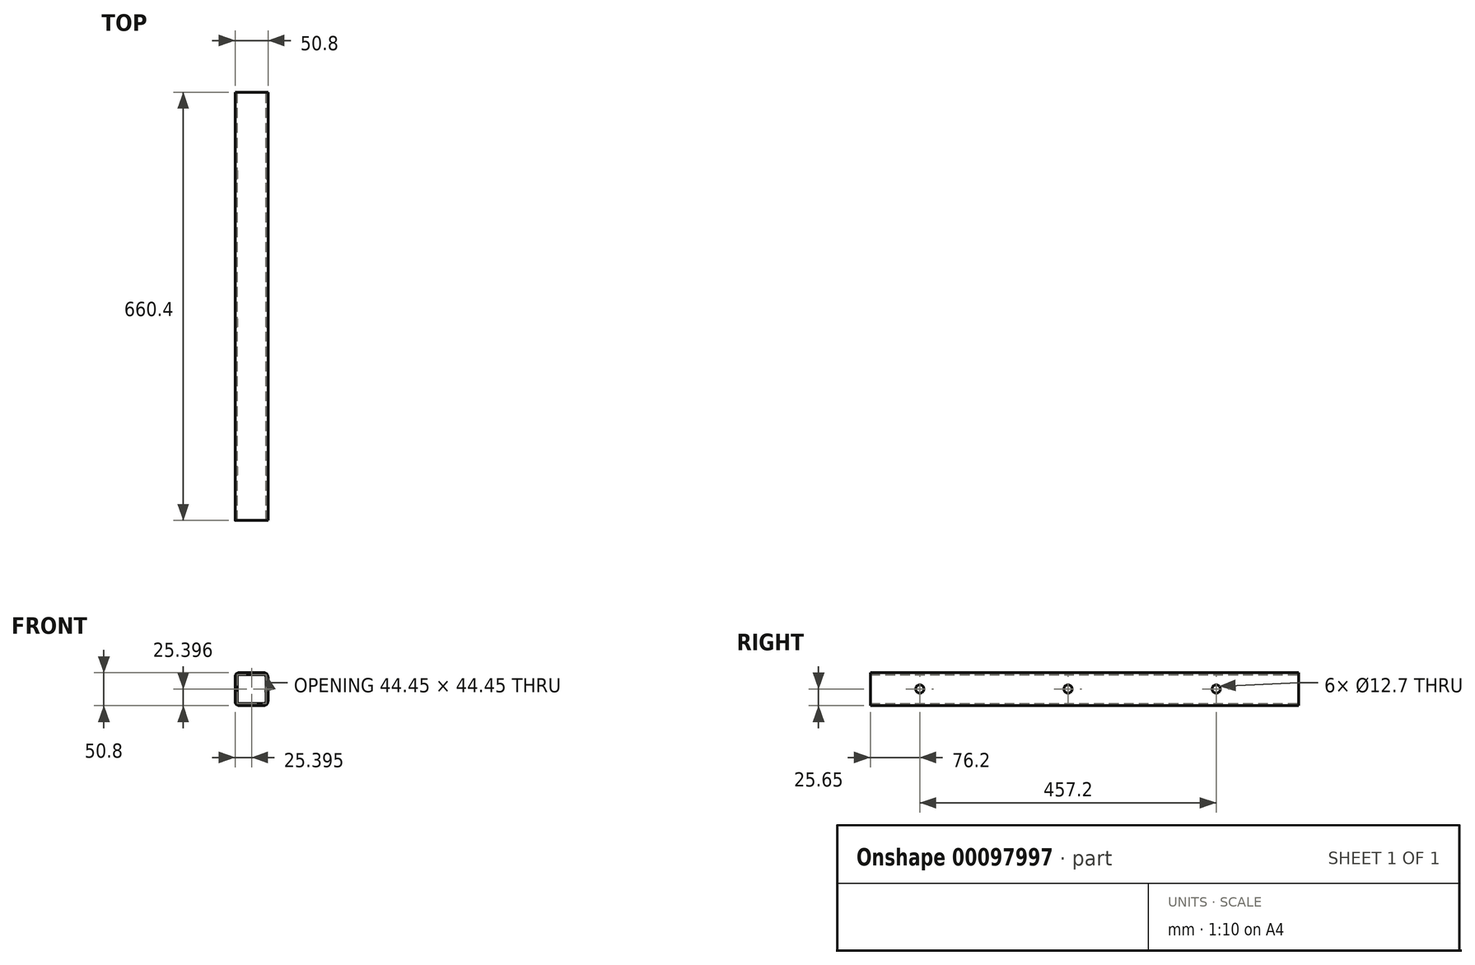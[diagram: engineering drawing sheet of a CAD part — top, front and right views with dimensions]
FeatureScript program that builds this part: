
annotation { "Feature Type Name" : "Feature", "Feature Type Description" : "" }
export const myFeature = defineFeature(function(context is Context, id is Id, definition is map)
    precondition{}
    {
        {
            var Q0;
            Q0=qCreatedBy(makeId("Front.planeOp"),FACE);
            var sketch = newSketch(context, id + "F0", { "sketchPlane" : qUnion([Q0])});
            skLineSegment(sketch, "E0.bottom", {"start": v(18.78, -25.65) * mm, "end": v(-19.32, -25.65) * mm});
            skLineSegment(sketch, "E0.top", {"start": v(18.78, 25.15) * mm, "end": v(-19.32, 25.15) * mm});
            skLineSegment(sketch, "E0.left", {"start": v(25.13, -19.3) * mm, "end": v(25.13, 18.8) * mm});
            skLineSegment(sketch, "E0.right", {"start": v(-25.67, -19.3) * mm, "end": v(-25.67, 18.8) * mm});
            skPoint(sketch, "E0.middle", {"position": v(-0.27, -0.25) * mm});
            skLineSegment(sketch, "E1.bottom", {"start": v(18.78, 21.97) * mm, "end": v(-19.32, 21.97) * mm});
            skLineSegment(sketch, "E1.top", {"start": v(18.78, -22.48) * mm, "end": v(-19.32, -22.48) * mm});
            skLineSegment(sketch, "E1.left", {"start": v(21.95, 18.8) * mm, "end": v(21.95, -19.3) * mm});
            skLineSegment(sketch, "E1.right", {"start": v(-22.5, 18.8) * mm, "end": v(-22.5, -19.3) * mm});
            skPoint(sketch, "E2.visualSharp", {"position": v(-25.67, 25.15) * mm});
            skArc(sketch, "E2.filletArc", {"start": v(-19.32, 25.15) * mm, "mid": v(-23.81, 23.29) * mm, "end": v(-25.67, 18.8) * mm});
            skPoint(sketch, "E3.visualSharp", {"position": v(25.13, 25.15) * mm});
            skArc(sketch, "E3.filletArc", {"start": v(25.13, 18.8) * mm, "mid": v(23.27, 23.29) * mm, "end": v(18.78, 25.15) * mm});
            skPoint(sketch, "E4.visualSharp", {"position": v(25.13, -25.65) * mm});
            skArc(sketch, "E4.filletArc", {"start": v(18.78, -25.65) * mm, "mid": v(23.27, -23.8) * mm, "end": v(25.13, -19.3) * mm});
            skPoint(sketch, "E5.visualSharp", {"position": v(-25.67, -25.65) * mm});
            skArc(sketch, "E5.filletArc", {"start": v(-25.67, -19.3) * mm, "mid": v(-23.81, -23.8) * mm, "end": v(-19.32, -25.65) * mm});
            skPoint(sketch, "E6.visualSharp", {"position": v(21.95, 21.97) * mm});
            skArc(sketch, "E6.filletArc", {"start": v(21.95, 18.8) * mm, "mid": v(21.02, 21.04) * mm, "end": v(18.78, 21.97) * mm});
            skPoint(sketch, "E7.visualSharp", {"position": v(21.95, -22.48) * mm});
            skArc(sketch, "E7.filletArc", {"start": v(18.78, -22.48) * mm, "mid": v(21.02, -21.55) * mm, "end": v(21.95, -19.3) * mm});
            skPoint(sketch, "E8.visualSharp", {"position": v(-22.5, -22.48) * mm});
            skArc(sketch, "E8.filletArc", {"start": v(-22.5, -19.3) * mm, "mid": v(-21.57, -21.55) * mm, "end": v(-19.32, -22.48) * mm});
            skPoint(sketch, "E9.visualSharp", {"position": v(-22.5, 21.97) * mm});
            skArc(sketch, "E9.filletArc", {"start": v(-19.32, 21.97) * mm, "mid": v(-21.57, 21.04) * mm, "end": v(-22.5, 18.8) * mm});
            skSolve(sketch);
        }
        {
            var Q0;
            Q0=makeQuery(id+"F0.imprint","IMPRINT",FACE,{"disambiguationData":[TD([[makeQuery(id+"F0.imprint","IMPRINT",EDGE,{"derivedFrom":sQuery(id+"F0.wireOp",EDGE,"E0.bottom")}),-1.0]])]});
            extrude(context, id + "F1", {"entities" : qUnion([Q0]), "endBound" : BoundingType.SYMMETRIC, "depth" : 660.4 * mm});
        }
        {
            var Q0;
            Q0=makeQuery(id+"F1.opExtrude","SWEPT_FACE",FACE,{"disambiguationData":[OSD([sQuery(id+"F0.wireOp",EDGE,"E0.left")])]});
            var sketch = newSketch(context, id + "F2", { "sketchPlane" : qUnion([Q0])});
            skCircle(sketch, "E10", {"center": v(-254, 0) * mm, "radius": 6.35 * mm});
            skCircle(sketch, "E11", {"center": v(203.2, 0) * mm, "radius": 6.35 * mm});
            skCircle(sketch, "E12", {"center": v(-25.4, 0) * mm, "radius": 6.35 * mm});
            skSolve(sketch);
        }
        {
            var Q0;
            Q0=makeQuery(id+"F2.imprint","IMPRINT",FACE,{"disambiguationData":[TD([[makeQuery(id+"F2.imprint","IMPRINT",EDGE,{"derivedFrom":sQuery(id+"F2.wireOp",EDGE,"E10")}),1.0]])]});
            var Q1;
            Q1=makeQuery(id+"F2.imprint","IMPRINT",FACE,{"disambiguationData":[TD([[makeQuery(id+"F2.imprint","IMPRINT",EDGE,{"derivedFrom":sQuery(id+"F2.wireOp",EDGE,"E11")}),1.0]])]});
            var Q2;
            Q2=makeQuery(id+"F2.imprint","IMPRINT",FACE,{"disambiguationData":[TD([[makeQuery(id+"F2.imprint","IMPRINT",EDGE,{"derivedFrom":sQuery(id+"F2.wireOp",EDGE,"E12")}),1.0]])]});
            extrude(context, id + "F3", {"entities" : qUnion([Q0, Q1, Q2]), "operationType" : NewBodyOperationType.REMOVE, "endBound" : BoundingType.THROUGH_ALL, "oppositeDirection" : true, "depth" : 25.4 * mm});
        }
    });
